# Revit family: Toilet_Lavatory-Rear_Mounted-Acorn-Euro_Urban-Neo_Metro-8951-W_Series
name_source: partatom
category: Plumbing Fixtures
units: mm (PartAtom-declared; Revit-internal decimal feet)

## family parameters
Cut with Voids When Loaded = No
Host = Face
OmniClass Number = 23.45.05.21.11.11
OmniClass Title = Water Operated Water Closets
Part Type = Normal
Room Calculation Point = No
Round Connector Dimension = Use Diameter
Shared = Yes

## types (8) — shared parameters
Assembly Code = D2010110
CW Connection = Yes
CWFU = 5
Cold Water Connection Diameter = 2 3/8"
Flush Rate = 1.6/0.8 GPF - 6.0/3.0 lpf
HW Connection = No
IAPMO Compliance = ASME A112.19.2M, CSA B45 Series
Length = 23"
Manufacturer = Neo-Metro
Product Documentation Link = https://www.neo-metro.com
Product Page URL = https://www.neo-metro.com
URL = http://www.neo-metro.com
Vent Connection = No
WFU = 5
Waste Connection = Yes
Waste Connection Diameter = 4"
Width = 14"
zero-valued in all types: HWFU

## per-type parameters (varying)
| type | ADA Compliant | ADA W 1 | ADA W 2 | Default Elevation | Description | Finish | Height | Material | OFF FLOOR | ON FLOOR |
| 8951-W-1 | No | No | No | 15 3/4" | Wall Supply, Off-Floor (Wall Waste), Satin  Finish Stainless Steel Toilet | Stainless Steel-Acorn-Satin Finish | 13 3/4" | Stainless Steel-Acorn-Satin Finish | Yes | No |
| 8951-W-1-HP | No | No | No | 15 3/4" | Wall Supply, Off-Floor (Wall Waste), Mira  High Polish Stainless Steel Toilet | Stainless Steel-Acorn-Mira-High Polish | 13 3/4" | Stainless Steel-Acorn-Mira-High Polish | Yes | No |
| 8951-W-2 | No | No | No | 15 3/4" | Wall Supply, On-Floor (Wall Waste), Satin  Finish Stainless Steel Toilet | Stainless Steel-Acorn-Satin Finish | 15 3/4" | Stainless Steel-Acorn-Satin Finish | No | Yes |
| 8951-ADA-W-2 | Yes | No | Yes | 17 3/4" | Wall Supply, On-Floor (Wall Waste), Mira  High Polish Stainless Steel Toilet | Stainless Steel-Acorn-Satin Finish | 17 3/4" | Stainless Steel-Acorn-Satin Finish | No | Yes |
| 8951-ADA-W-1 | Yes | Yes | No | 18" | Wall Supply, Off-Floor (Wall Waste), Mira  High Polish Stainless Steel Toilet | Stainless Steel-Acorn-Satin Finish | 13 3/4" | Stainless Steel-Acorn-Satin Finish | Yes | No |
| 8951-ADA-W-2-HP | Yes | No | Yes | 17 3/4" | Wall Supply, On-Floor (Wall Waste), Mira  High Polish Stainless Steel Toilet | Stainless Steel-Acorn-Mira-High Polish | 17 3/4" | Stainless Steel-Acorn-Mira-High Polish | No | Yes |
| 8951-ADA-W-1-HP | Yes | Yes | No | 18" | Wall Supply, Off-Floor (Wall Waste), Mira  High Polish Stainless Steel Toilet | Stainless Steel-Acorn-Mira-High Polish | 13 3/4" | Stainless Steel-Acorn-Mira-High Polish | Yes | No |
| 8951-W-2-HP | No | No | No | 15 3/4" | Wall Supply, On-Floor (Wall Waste), Satin  Finish Stainless Steel Toilet | Stainless Steel-Acorn-Mira-High Polish | 15 3/4" | Stainless Steel-Acorn-Mira-High Polish | No | Yes |

note: column(s) folded — value = type name in every type: Model

## geometry (parser evidence)
native form markers: Sweep x3
no freeform markers — native parametric forms only
